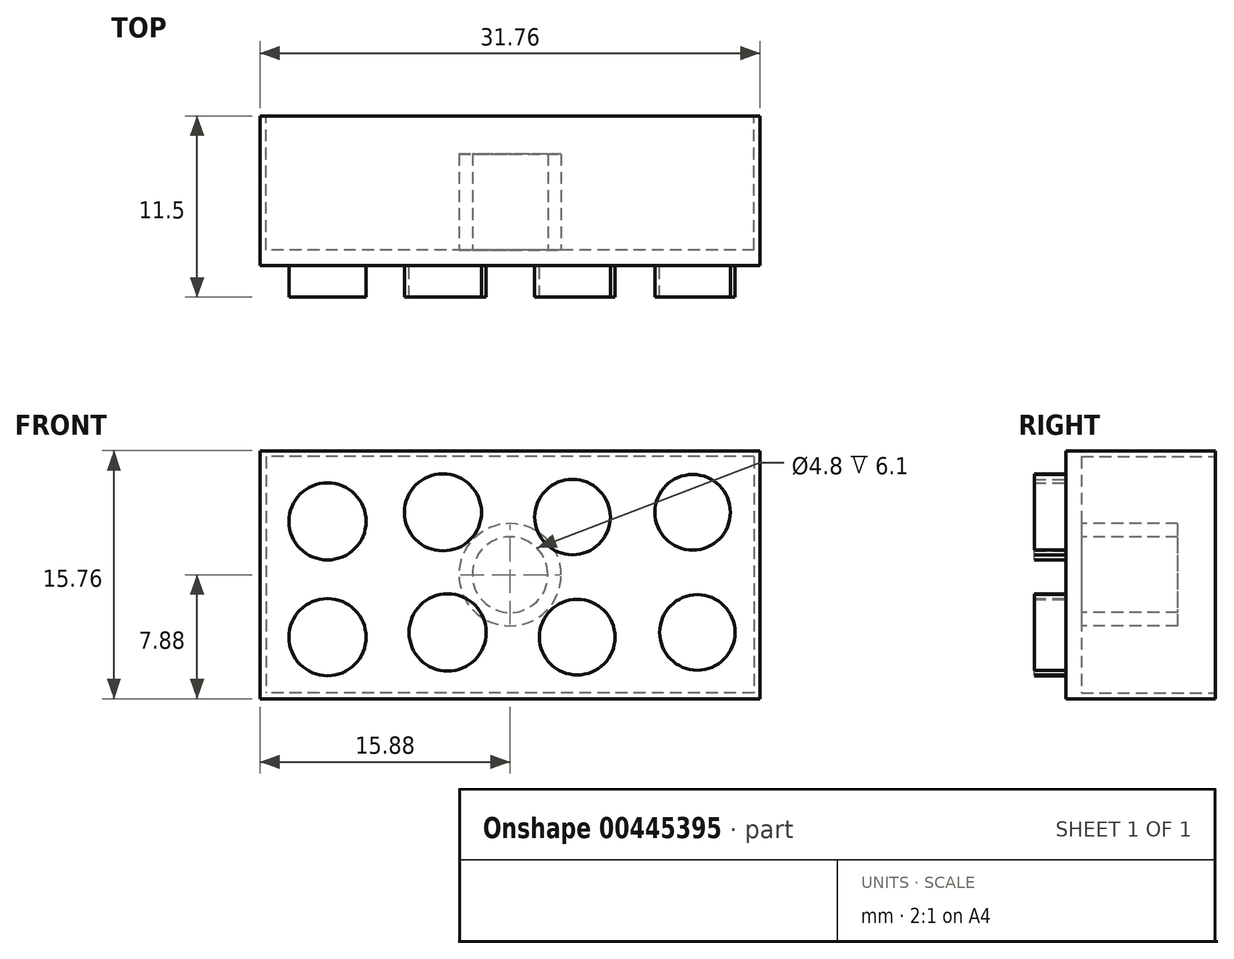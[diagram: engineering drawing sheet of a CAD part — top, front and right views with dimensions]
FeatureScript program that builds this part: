
annotation { "Feature Type Name" : "Feature", "Feature Type Description" : "" }
export const myFeature = defineFeature(function(context is Context, id is Id, definition is map)
    precondition{}
    {
        {
            var Q0;
            Q0=qCreatedBy(makeId("Front.planeOp"),FACE);
            var sketch = newSketch(context, id + "F0", { "sketchPlane" : qUnion([Q0])});
            skLineSegment(sketch, "E0.bottom", {"start": v(15.88, -7.88) * mm, "end": v(-15.88, -7.88) * mm});
            skLineSegment(sketch, "E0.top", {"start": v(15.88, 7.88) * mm, "end": v(-15.88, 7.87) * mm});
            skLineSegment(sketch, "E0.left", {"start": v(15.88, -7.88) * mm, "end": v(15.88, 7.88) * mm});
            skLineSegment(sketch, "E0.right", {"start": v(-15.88, -7.88) * mm, "end": v(-15.88, 7.87) * mm});
            skPoint(sketch, "E0.middle", {"position": v(0, 0) * mm});
            skSolve(sketch);
        }
        {
            var Q0;
            Q0=makeQuery(id+"F0.imprint","IMPRINT",FACE,{"disambiguationData":[TD([[makeQuery(id+"F0.imprint","IMPRINT",EDGE,{"derivedFrom":sQuery(id+"F0.wireOp",EDGE,"E0.bottom")}),-1.0]])]});
            extrude(context, id + "F1", {"entities" : qUnion([Q0]), "depth" : 9.5 * mm});
        }
        {
            var Q0;
            Q0=makeQuery(id+"F1.opExtrude","CAP_FACE",FACE,{"disambiguationData":[OSD([sQuery(id+"F0.wireOp",EDGE,"E0.bottom"),sQuery(id+"F0.wireOp",EDGE,"E0.top"),sQuery(id+"F0.wireOp",EDGE,"E0.left"),sQuery(id+"F0.wireOp",EDGE,"E0.right")])],"isStart":true});
            var sketch = newSketch(context, id + "F2", { "sketchPlane" : qUnion([Q0])});
            skLineSegment(sketch, "E1.bottom", {"start": v(-15.5, 7.5) * mm, "end": v(15.5, 7.5) * mm});
            skLineSegment(sketch, "E1.top", {"start": v(-15.5, -7.5) * mm, "end": v(15.5, -7.5) * mm});
            skLineSegment(sketch, "E1.left", {"start": v(-15.5, 7.5) * mm, "end": v(-15.5, -7.5) * mm});
            skLineSegment(sketch, "E1.right", {"start": v(15.5, 7.5) * mm, "end": v(15.5, -7.5) * mm});
            skPoint(sketch, "E1.middle", {"position": v(0, 0) * mm});
            skSolve(sketch);
        }
        {
            var Q0;
            Q0=makeQuery(id+"F2.imprint","IMPRINT",FACE,{"disambiguationData":[TD([[makeQuery(id+"F2.imprint","IMPRINT",EDGE,{"derivedFrom":sQuery(id+"F2.wireOp",EDGE,"E1.bottom")}),-1.0]])]});
            extrude(context, id + "F3", {"entities" : qUnion([Q0]), "operationType" : NewBodyOperationType.REMOVE, "oppositeDirection" : true, "depth" : 8.5 * mm});
        }
        {
            var Q0;
            Q0=makeQuery(id+"F1.opExtrude","CAP_FACE",FACE,{"disambiguationData":[OSD([sQuery(id+"F0.wireOp",EDGE,"E0.bottom"),sQuery(id+"F0.wireOp",EDGE,"E0.top"),sQuery(id+"F0.wireOp",EDGE,"E0.left"),sQuery(id+"F0.wireOp",EDGE,"E0.right")])],"isStart":false});
            var sketch = newSketch(context, id + "F4", { "sketchPlane" : qUnion([Q0])});
            skLineSegment(sketch, "E2", {"start": v(0, 0) * mm, "end": v(-7.93, 0) * mm});
            skLineSegment(sketch, "E3", {"start": v(0, 0) * mm, "end": v(7.93, 0) * mm});
            skLineSegment(sketch, "E4", {"start": v(-7.93, 0) * mm, "end": v(-4.26, 3.96) * mm});
            skLineSegment(sketch, "E5", {"start": v(-4.26, 3.96) * mm, "end": v(-7.93, 0) * mm});
            skLineSegment(sketch, "E6", {"start": v(-7.93, 0) * mm, "end": v(-11.6, 3.39) * mm});
            skLineSegment(sketch, "E7", {"start": v(-11.6, 3.39) * mm, "end": v(-7.93, 0) * mm});
            skLineSegment(sketch, "E8", {"start": v(-7.93, 0) * mm, "end": v(-11.6, -3.96) * mm});
            skLineSegment(sketch, "E9", {"start": v(-11.6, -3.97) * mm, "end": v(-7.93, 0) * mm});
            skLineSegment(sketch, "E10", {"start": v(-7.93, 0) * mm, "end": v(-3.96, -3.67) * mm});
            skPoint(sketch, "E10.endSnap0", {"position": v(-3.96, 0) * mm});
            skCircle(sketch, "E11", {"center": v(-11.6, 3.39) * mm, "radius": 2.45 * mm});
            skCircle(sketch, "E12", {"center": v(-4.26, 3.96) * mm, "radius": 2.45 * mm});
            skCircle(sketch, "E13", {"center": v(-3.96, -3.67) * mm, "radius": 2.45 * mm});
            skCircle(sketch, "E14", {"center": v(-11.6, -3.96) * mm, "radius": 2.45 * mm});
            skLineSegment(sketch, "E15", {"start": v(7.93, 0) * mm, "end": v(11.6, 3.97) * mm});
            skLineSegment(sketch, "E16", {"start": v(11.6, 3.97) * mm, "end": v(7.93, 0) * mm});
            skLineSegment(sketch, "E17", {"start": v(7.93, 0) * mm, "end": v(3.96, 3.67) * mm});
            skPoint(sketch, "E17.endSnap0", {"position": v(3.96, 0) * mm});
            skLineSegment(sketch, "E18", {"start": v(3.97, 3.67) * mm, "end": v(7.93, 0) * mm});
            skLineSegment(sketch, "E19", {"start": v(7.93, 0) * mm, "end": v(4.26, -3.97) * mm});
            skLineSegment(sketch, "E20", {"start": v(4.26, -3.97) * mm, "end": v(7.93, 0) * mm});
            skLineSegment(sketch, "E21", {"start": v(7.93, 0) * mm, "end": v(11.9, -3.67) * mm});
            skCircle(sketch, "E22", {"center": v(3.97, 3.67) * mm, "radius": 2.4 * mm});
            skCircle(sketch, "E23", {"center": v(11.6, 3.97) * mm, "radius": 2.4 * mm});
            skCircle(sketch, "E24", {"center": v(11.9, -3.67) * mm, "radius": 2.4 * mm});
            skCircle(sketch, "E25", {"center": v(4.26, -3.97) * mm, "radius": 2.4 * mm});
            skSolve(sketch);
        }
        {
            var Q0;
            Q0 = qSketchRegion(id + "F4", true);
            extrude(context, id + "F5", {"entities" : qUnion([Q0]), "operationType" : NewBodyOperationType.ADD, "depth" : 2 * mm});
        }
        {
            var Q0;
            Q0=makeQuery(id+"F3.boolean.opBoolean","COPY",FACE,{"derivedFrom":makeQuery(id+"F3.opExtrude","CAP_FACE",FACE,{"disambiguationData":[OSD([sQuery(id+"F2.wireOp",EDGE,"E1.bottom"),sQuery(id+"F2.wireOp",EDGE,"E1.top"),sQuery(id+"F2.wireOp",EDGE,"E1.left"),sQuery(id+"F2.wireOp",EDGE,"E1.right")])],"isStart":false})});
            var sketch = newSketch(context, id + "F6", { "sketchPlane" : qUnion([Q0])});
            skCircle(sketch, "E26", {"center": v(0, 0) * mm, "radius": 3.25 * mm});
            skCircle(sketch, "E27", {"center": v(0, 0) * mm, "radius": 2.4 * mm});
            skLineSegment(sketch, "E28", {"start": v(0, -3.25) * mm, "end": v(0, -7.5) * mm});
            skLineSegment(sketch, "E29", {"start": v(0, 3.25) * mm, "end": v(0, 7.5) * mm});
            skSolve(sketch);
        }
        {
            var Q0;
            Q0 = qSketchRegion(id + "F6", true);
            extrude(context, id + "F7", {"entities" : qUnion([Q0]), "operationType" : NewBodyOperationType.ADD, "depth" : 6.1 * mm});
        }
    });
